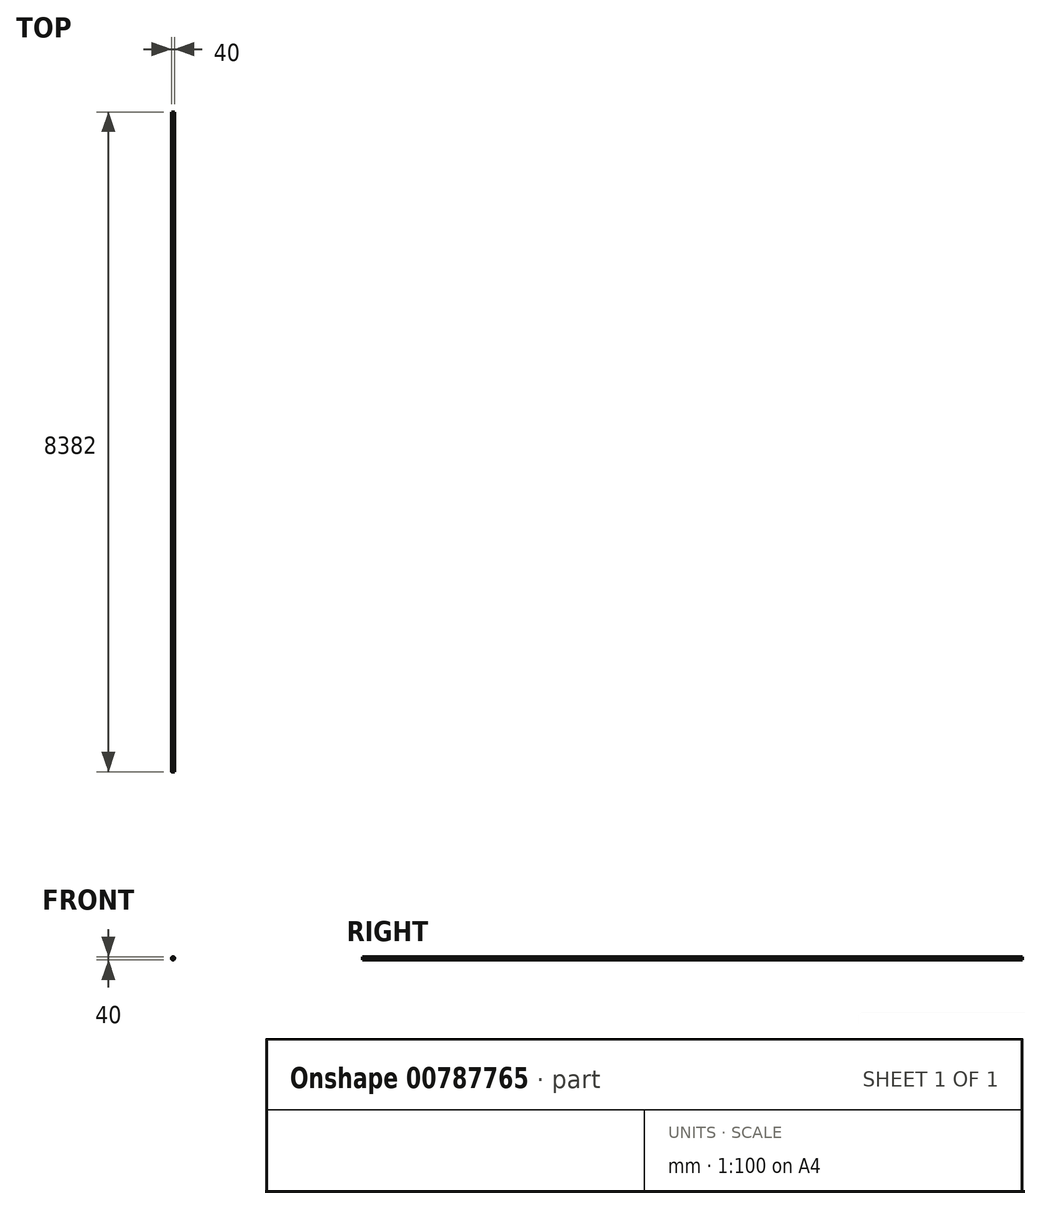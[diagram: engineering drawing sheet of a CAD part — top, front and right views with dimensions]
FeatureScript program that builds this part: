
annotation { "Feature Type Name" : "Feature", "Feature Type Description" : "" }
export const myFeature = defineFeature(function(context is Context, id is Id, definition is map)
    precondition{}
    {
        {
            var Q0;
            Q0=qCreatedBy(makeId("Front.planeOp"),FACE);
            var sketch = newSketch(context, id + "F0", { "sketchPlane" : qUnion([Q0])});
            skCircle(sketch, "E0", {"center": v(0, 0) * mm, "radius": 20 * mm});
            skSolve(sketch);
        }
        {
            var Q0;
            Q0 = qSketchRegion(id + "F0", true);
            extrude(context, id + "F1", {"entities" : qUnion([Q0]), "depth" : 8382 * mm, "offsetDistance" : 25 * mm});
        }
    });
